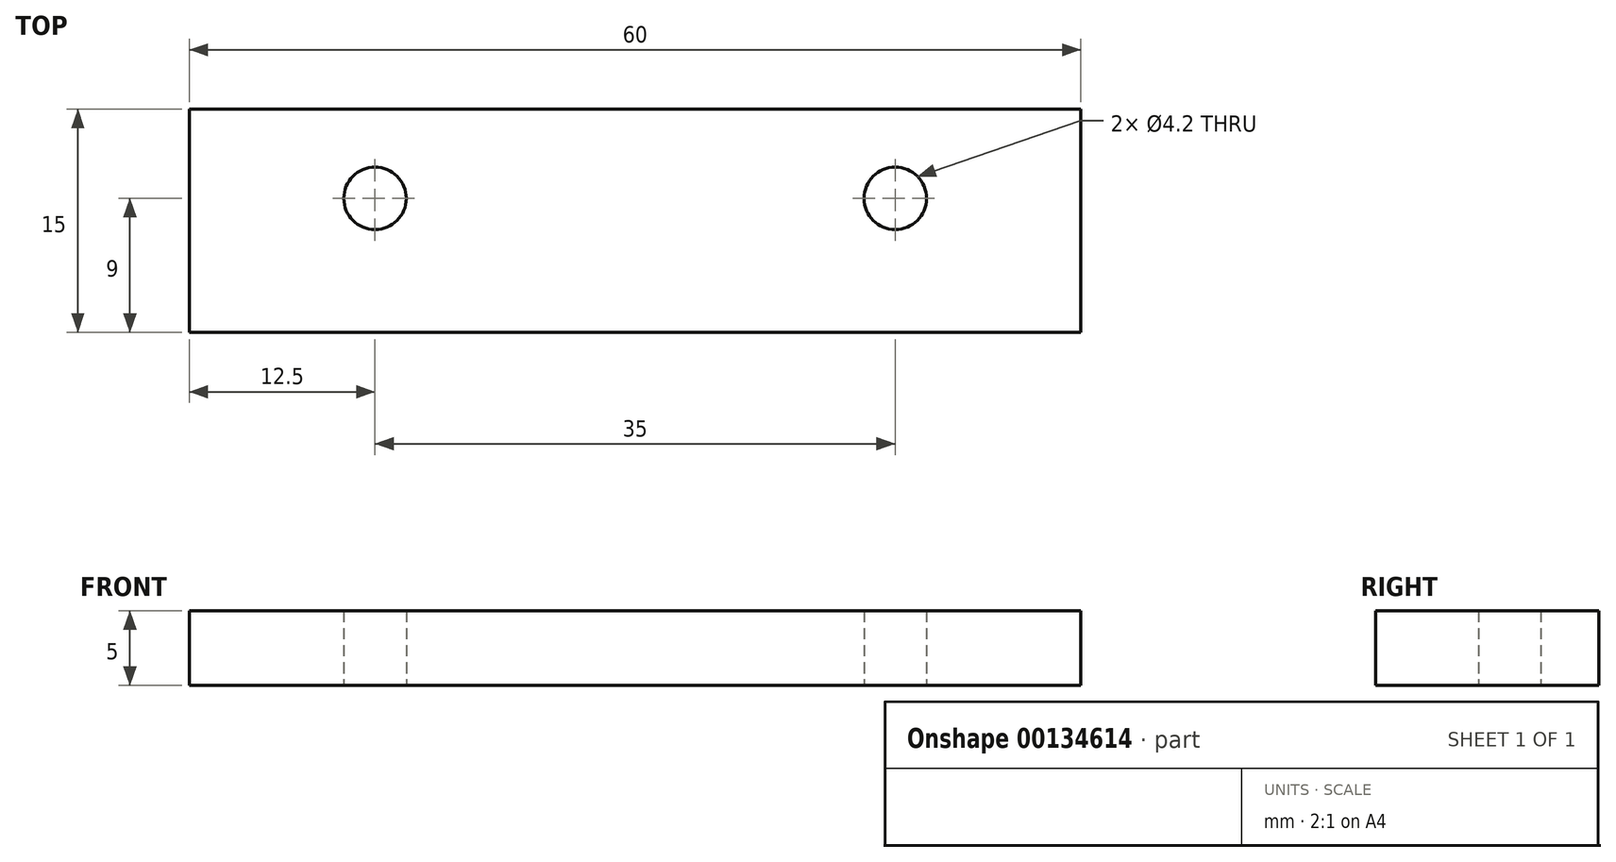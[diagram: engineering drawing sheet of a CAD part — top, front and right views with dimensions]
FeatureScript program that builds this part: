
annotation { "Feature Type Name" : "Feature", "Feature Type Description" : "" }
export const myFeature = defineFeature(function(context is Context, id is Id, definition is map)
    precondition{}
    {
        {
            var Q0;
            Q0=qCreatedBy(makeId("Top.planeOp"),FACE);
            var sketch = newSketch(context, id + "F0", { "sketchPlane" : qUnion([Q0])});
            skLineSegment(sketch, "E0.bottom", {"start": v(30, -7.5) * mm, "end": v(-30, -7.5) * mm});
            skLineSegment(sketch, "E0.top", {"start": v(30, 7.5) * mm, "end": v(-30, 7.5) * mm});
            skLineSegment(sketch, "E0.left", {"start": v(30, -7.5) * mm, "end": v(30, 7.5) * mm});
            skLineSegment(sketch, "E0.right", {"start": v(-30, -7.5) * mm, "end": v(-30, 7.5) * mm});
            skPoint(sketch, "E0.middle", {"position": v(0, 0) * mm});
            skCircle(sketch, "E1", {"center": v(-17.5, 1.5) * mm, "radius": 2.1 * mm});
            skCircle(sketch, "E2", {"center": v(17.5, 1.5) * mm, "radius": 2.1 * mm});
            skLineSegment(sketch, "E3", {"start": v(0, 7.5) * mm, "end": v(0, -7.5) * mm, "construction": true});
            skSolve(sketch);
        }
        {
            var Q0;
            Q0=makeQuery(id+"F0.imprint","IMPRINT",FACE,{"disambiguationData":[TD([[makeQuery(id+"F0.imprint","IMPRINT",EDGE,{"derivedFrom":sQuery(id+"F0.wireOp",EDGE,"E0.bottom")}),-1.0]])]});
            extrude(context, id + "F1", {"entities" : qUnion([Q0]), "depth" : 5 * mm});
        }
    });
